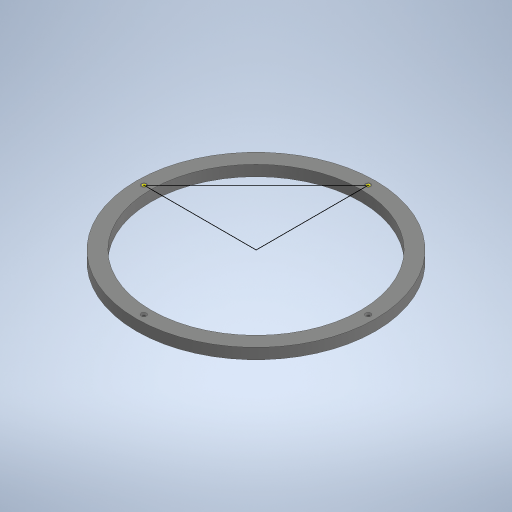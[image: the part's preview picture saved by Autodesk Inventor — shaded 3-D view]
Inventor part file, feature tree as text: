
AUTODESK INVENTOR PART (.ipt)
format: ipt  version: 2023 (Build 270158000, 158)  size: 273,408 bytes
history: native  units: in
note: dims shown in document units (in); Inventor stores cm internally (conversion verified against a paired STEP export)
features: sketch x3, extrude x1, hole x1, pattern_circular x1
ambient origin geometry x8: Origin, YZ Plane, XZ Plane, XY Plane, X Axis, Y Axis, Z Axis, Center Point
bodies: Solid1 (feature_tree)
feature tree (6):
  extrude  "Extrusion1"  Depth=8.7598in
  hole  "Hole1"  [1 undecoded]
  pattern_circular  "Circular Pattern1"  Count=4 Angle=360.0deg
  sketch  "Sketch3"  dims[d5=0.0984in d6=0.2362in d7=0.1969in d8=0.0787in d9=90.0deg d10=0.315in d11=0.8108in d12=1.5748in d13=360.0deg]
  sketch  "Sketch1"  dims[d0=7.6772in d1=8.7598in]
  sketch  "Sketch2"  dims[d2=0.3937in d3=0.0in d4=4.1093in]
note: 1 required parameter value undecoded (feature->parameter linkage not recoverable at this tier; creation-order binding heuristic only, values carry confidence <= 0.55)
